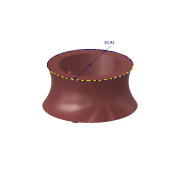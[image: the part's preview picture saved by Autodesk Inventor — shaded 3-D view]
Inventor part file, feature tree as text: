
AUTODESK INVENTOR PART (.ipt)
format: ipt  version: 2018 (Build 220112000, 112)  size: 326,144 bytes
history: native  units: mm
features: sketch x19, extrude x15, plane x3, fillet x3, pattern_circular x2, loft x1, projected_geometry x1
ambient origin geometry x8: Origin, YZ Plane, XZ Plane, XY Plane, X Axis, Y Axis, Z Axis, Center Point
bodies: Solid1 (feature_tree)
feature tree (44):
  extrude  "Extrusion1"  Depth=4.0mm TaperAngle=0.0deg
  extrude  "Extrusion2"  Depth=29.7mm
  pattern_circular  "Circular Pattern1"  Count=3 Angle=360.0deg
  extrude  "Extrusion3"  Depth=2.5mm
  pattern_circular  "Circular Pattern2"  Count=3 Angle=360.0deg
  extrude  "Extrusion4"  Depth=4.0mm TaperAngle=0.0deg
  extrude  "Extrusion5"  Depth=7.25mm
  extrude  "Extrusion6"  Depth=0.4mm TaperAngle=0.0deg
  plane  "Work Plane3"
  loft  "Loft1"
  extrude  "Extrusion7"  Depth=30.0mm
  extrude  "Extrusion8"  TaperAngle=0.0deg  [1 undecoded]
  extrude  "Extrusion9"  TaperAngle=0.0deg  [1 undecoded]
  extrude  "Extrusion10"  Depth=12.0mm TaperAngle=0.0deg
  fillet  "Fillet2"  Radius=5.35mm
  fillet  "Fillet3"  Radius=7.25mm
  extrude  "Extrusion11"  Depth=0.4mm TaperAngle=0.0deg
  extrude  "Extrusion13"  Depth=1.0mm
  fillet  "Fillet4"  Radius=1.0mm
  extrude  "Extrusion14"  Depth=14.0mm
  extrude  "Extrusion15"  Depth=25.0mm
  extrude  "Extrusion16"  Depth=2.0mm
  sketch  "Sketch19"  dims[d61=15.0mm d62=0.0mm d63=2.0mm d64=3.0mm d65=0.0mm d66=0.0mm d67=3.5mm d68=0.0mm d69=3.5mm d70=0.0mm d71=33.429993mm]
  sketch  "Sketch1"  dims[d0=20.6114mm d1=4.0mm d2=0.0mm]
  sketch  "Sketch2"  dims[d3=20.6114mm d4=29.7mm]
  sketch  "Sketch3"  dims[d5=4.0mm d6=0.0mm d7=30.0mm d8=360.0deg]
  sketch  "Sketch4"  dims[d10=2.5mm d11=1.25mm]
  sketch  "Sketch5"  dims[d12=7.5443mm]
  sketch  "Sketch6"  dims[d13=4.0mm d14=0.0mm d15=30.0mm d16=360.0deg]
  plane  "Work Plane1"
  plane  "Work Plane2"
  sketch  "Sketch7"  dims[d18=2.3mm d19=4.0mm d20=0.0mm]
  sketch  "Sketch8"  dims[d21=5.25mm d22=7.25mm]
  sketch  "Sketch9"  dims[d23=2.9mm d24=0.0mm d25=0.4mm d26=0.0mm]
  sketch  "Sketch10"  dims[d27=0.0mm d28=10.0mm d29=10.0mm]
  sketch  "Sketch11"  dims[d30=37.0mm d31=30.0mm]
  sketch  "Sketch12"  dims[d32=37.0mm d33=0.0mm d34=90.0deg]
  sketch  "Sketch13"  dims[d35=0.0mm d36=90.0deg d37=0.0mm d38=90.0deg]
  sketch  "Sketch14"  dims[d39=12.0mm d40=20.0mm d41=0.0mm d42=5.35mm d43=7.25mm]
  sketch  "Sketch15"  dims[d44=2.9mm d45=0.0mm d46=0.4mm d47=0.0mm]
  sketch  "Sketch16"  dims[d48=0.0mm d49=0.0mm d51=1.0mm d52=1.0mm]
  sketch  "Sketch17"  dims[d53=2.0mm d54=14.0mm]
  sketch  "Sketch18"  dims[d55=0.4mm d56=0.0mm d57=25.0mm]
  projected_geometry  "Projected Loop1"
note: 2 required parameter values undecoded (feature->parameter linkage not recoverable at this tier; creation-order binding heuristic only, values carry confidence <= 0.55)
